# Revit family: ASL_Designline_64_Timber_Door_40mm_Jamb
name_source: partatom
category: Detail Items
revit_build: Autodesk Revit 2018 (Build: 20170223_1515(x64)
units: mm (PartAtom-declared; Revit-internal decimal feet)

## family parameters
Rotate with component = No
Section Shape = Not Defined
Shared = Yes

## types (4) — shared parameters
13mm Plasterboard = Yes
18mm Plasterboard = No
ASL 410 = No
Manufacturer = Aluminate Solutions Limited
Masking Region Parametric = 52 mm
Technical Info = www.aluminate.nz

## per-type parameters (varying)
| type | 40mm Door Jamb Standard | ASL 400 | ASL 407 | Door_40 | Glazing | Hinge_Single | Plasterboard Head Parametric | Type Comments |
| ASL 400 Single Action Door 40mm | Yes | Yes | No | Yes | No | Yes | 7 mm  [stored 0.0229659 ft] | ASL Designline ASL 400 Jamb With Single Action 40mm Timber Door |
| ASL 400 Glazing | No | Yes | No | No | Yes | No | 7 mm  [stored 0.0229659 ft] | ASL Designline ASL 400 Jamb With Glazing |
| ASL 407 Shadowline Single Action Door 40mm | Yes | No | Yes | Yes | No | Yes | 20 mm  [stored 0.0656168 ft] | ASL Designline ASL 407 Shadowline Jamb With Single Action 40mm Timber Door |
| ASL 407 Shadowline Glazing | No | No | Yes | No | Yes | No | 20 mm  [stored 0.0656168 ft] | ASL Designline ASL 407 Shadowline Jamb With Glazing |

note: [stored X ft] marks values corroborated as IEEE doubles in the binary element streams (Revit-internal decimal feet)

## geometry (parser evidence)
native form markers: Sweep x9
no freeform markers — native parametric forms only
